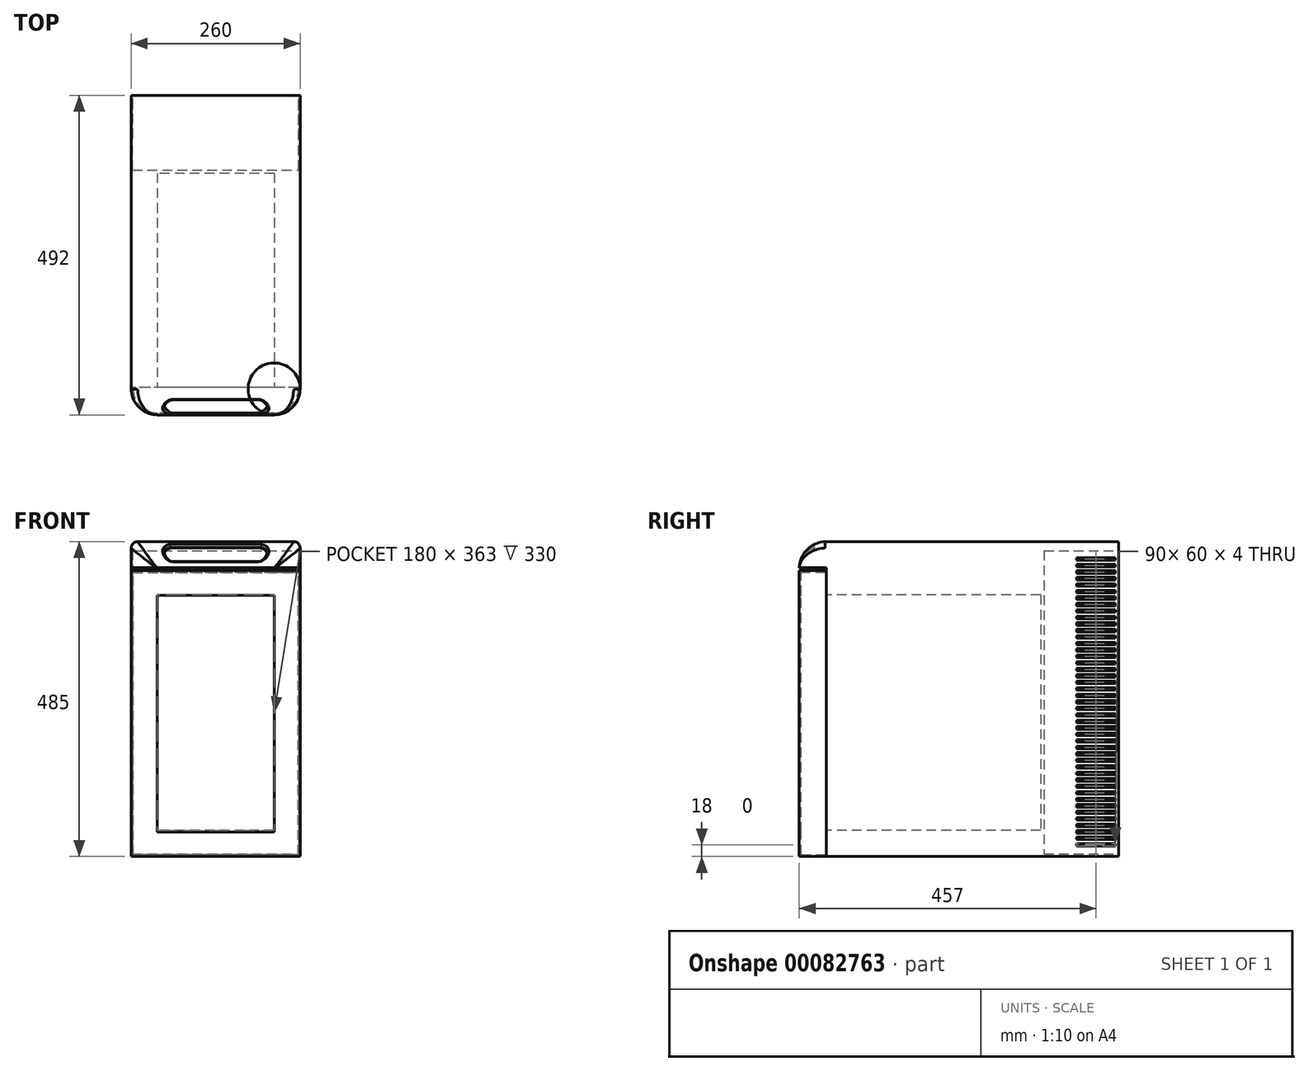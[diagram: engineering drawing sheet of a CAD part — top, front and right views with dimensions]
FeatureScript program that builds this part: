
annotation { "Feature Type Name" : "Feature", "Feature Type Description" : "" }
export const myFeature = defineFeature(function(context is Context, id is Id, definition is map)
    precondition{}
    {
        {
            var Q0;
            Q0=qCreatedBy(makeId("Top.planeOp"),FACE);
            var sketch = newSketch(context, id + "F0", { "sketchPlane" : qUnion([Q0])});
            skLineSegment(sketch, "E0.bottom", {"start": v(130, 225) * mm, "end": v(-130, 225) * mm});
            skLineSegment(sketch, "E0.top", {"start": v(130, -225) * mm, "end": v(-130, -225) * mm});
            skLineSegment(sketch, "E0.left", {"start": v(130, 225) * mm, "end": v(130, -225) * mm});
            skLineSegment(sketch, "E0.right", {"start": v(-130, 225) * mm, "end": v(-130, -225) * mm});
            skPoint(sketch, "E0.middle", {"position": v(0, 0) * mm});
            skSolve(sketch);
        }
        {
            var Q0;
            Q0 = qSketchRegion(id + "F0", true);
            extrude(context, id + "F1", {"entities" : qUnion([Q0]), "depth" : 485 * mm});
        }
        {
            var Q0;
            Q0=makeQuery(id+"F1.opExtrude","SWEPT_FACE",FACE,{"disambiguationData":[OSD([sQuery(id+"F0.wireOp",EDGE,"E0.right")])]});
            var sketch = newSketch(context, id + "F2", { "sketchPlane" : qUnion([Q0])});
            skLineSegment(sketch, "E1", {"start": v(225, 445) * mm, "end": v(267, 445) * mm});
            skLineSegment(sketch, "E2", {"start": v(225, 445) * mm, "end": v(225, 485) * mm});
            skLineSegment(sketch, "E3", {"start": v(225, 485) * mm, "end": v(-225, 485) * mm, "construction": true});
            skArc(sketch, "E4", {"start": v(225, 485) * mm, "mid": v(254, 473.4) * mm, "end": v(267, 445) * mm});
            skSolve(sketch);
        }
        {
            var Q0;
            Q0 = qSketchRegion(id + "F2", true);
            var Q1;
            Q1=makeQuery(id+"F1.opExtrude","SWEPT_FACE",FACE,{"disambiguationData":[OSD([sQuery(id+"F0.wireOp",EDGE,"E0.left")])]});
            extrude(context, id + "F3", {"entities" : qUnion([Q0]), "operationType" : NewBodyOperationType.ADD, "endBound" : BoundingType.UP_TO_SURFACE, "oppositeDirection" : true, "endBoundEntityFace" : qUnion([Q1]), "depth" : 25 * mm});
        }
        {
            var Q0;
            Q0=makeQuery(id+"F3.opExtrude","SWEPT_FACE",FACE,{"disambiguationData":[OSD([sQuery(id+"F2.wireOp",EDGE,"E1")])]});
            var sketch = newSketch(context, id + "F4", { "sketchPlane" : qUnion([Q0])});
            skLineSegment(sketch, "E5", {"start": v(0, 225) * mm, "end": v(0, 267) * mm, "construction": true});
            skArc(sketch, "E6", {"start": v(-130, 227) * mm, "mid": v(-118.28, 255.28) * mm, "end": v(-90, 267) * mm});
            skLineSegment(sketch, "E7", {"start": v(-130, 227) * mm, "end": v(-130, 267) * mm});
            skLineSegment(sketch, "E8", {"start": v(-130, 267) * mm, "end": v(-90, 267) * mm});
            skArc(sketch, "E9.MirrorCS", {"start": v(130, 227) * mm, "mid": v(118.28, 255.28) * mm, "end": v(90, 267) * mm});
            skLineSegment(sketch, "E10.MirrorCS", {"start": v(130, 227) * mm, "end": v(130, 267) * mm});
            skLineSegment(sketch, "E11.MirrorCS", {"start": v(130, 267) * mm, "end": v(90, 267) * mm});
            skSolve(sketch);
        }
        {
            var Q0;
            Q0 = qSketchRegion(id + "F4", true);
            extrude(context, id + "F5", {"entities" : qUnion([Q0]), "operationType" : NewBodyOperationType.REMOVE, "endBound" : BoundingType.THROUGH_ALL, "oppositeDirection" : true, "depth" : 25 * mm});
        }
        {
            var Q0;
            Q0=makeQuery(id+"F3.opExtrude","CAP_EDGE",EDGE,{"disambiguationData":[OSD([sQuery(id+"F2.wireOp",EDGE,"E4")])],"isStart":true});
            var Q1;
            Q1=makeQuery(id+"F5.boolean.opBoolean","INTERSECT",EDGE,{"derivedFrom":[makeQuery(id+"F3.opExtrude","SWEPT_FACE",FACE,{"disambiguationData":[OSD([sQuery(id+"F2.wireOp",EDGE,"E4")])]}),makeQuery(id+"F5.opExtrude","SWEPT_FACE",FACE,{"disambiguationData":[OSD([sQuery(id+"F4.wireOp",EDGE,"E6")])]})]});
            var Q2;
            Q2=makeQuery(id+"F3.opExtrude","CAP_EDGE",EDGE,{"disambiguationData":[OSD([sQuery(id+"F2.wireOp",EDGE,"E4")])],"isStart":false});
            var Q3;
            Q3=makeQuery(id+"F5.boolean.opBoolean","INTERSECT",EDGE,{"derivedFrom":[makeQuery(id+"F3.opExtrude","SWEPT_FACE",FACE,{"disambiguationData":[OSD([sQuery(id+"F2.wireOp",EDGE,"E4")])]}),makeQuery(id+"F5.opExtrude","SWEPT_FACE",FACE,{"disambiguationData":[OSD([sQuery(id+"F4.wireOp",EDGE,"E9.MirrorCS")])]})]});
            var Q4;
            Q4=makeQuery(id+"F1.opExtrude","CAP_EDGE",EDGE,{"disambiguationData":[OSD([sQuery(id+"F0.wireOp",EDGE,"E0.right")])],"isStart":false});
            var Q5;
            Q5=makeQuery(id+"F1.opExtrude","CAP_EDGE",EDGE,{"disambiguationData":[OSD([sQuery(id+"F0.wireOp",EDGE,"E0.left")])],"isStart":false});
            fillet(context, id + "F6", {"entities" : qUnion([Q0, Q1, Q2, Q3, Q4, Q5]), "radius" : 10 * mm, "allowEdgeOverflow" : false});
        }
        {
            var Q0;
            Q0=makeQuery(id+"F3.opExtrude","SWEPT_FACE",FACE,{"disambiguationData":[OSD([sQuery(id+"F2.wireOp",EDGE,"E1")])]});
            cPlane(context, id + "F7", {"entities" : qUnion([Q0]), "cplaneType" : CPlaneType.OFFSET, "offset" : 5 * mm, "width" : 150 * mm, "height" : 150 * mm});
        }
        {
            var Q0;
            Q0=qCreatedBy(id+"F7.planeOp",FACE);
            var sketch = newSketch(context, id + "F8", { "sketchPlane" : qUnion([Q0])});
            skLineSegment(sketch, "E12.0", {"start": v(90, 267) * mm, "end": v(-90, 267) * mm});
            skArc(sketch, "E12.1", {"start": v(130, 227) * mm, "mid": v(118.74, 254.82) * mm, "end": v(91.3, 266.98) * mm});
            skArc(sketch, "E12.2", {"start": v(91.3, 266.98) * mm, "mid": v(90.65, 267) * mm, "end": v(90, 267) * mm});
            skArc(sketch, "E12.3", {"start": v(-130, 227) * mm, "mid": v(-118.74, 254.82) * mm, "end": v(-91.3, 266.98) * mm});
            skArc(sketch, "E12.4", {"start": v(-91.3, 266.98) * mm, "mid": v(-90.65, 267) * mm, "end": v(-90, 267) * mm});
            skLineSegment(sketch, "E12.5", {"start": v(-130, 225) * mm, "end": v(-130, 227) * mm});
            skLineSegment(sketch, "E12.6", {"start": v(130, 225) * mm, "end": v(130, 227) * mm});
            skLineSegment(sketch, "E13", {"start": v(-130, 225) * mm, "end": v(130, 225) * mm});
            skSolve(sketch);
        }
        {
            var Q0;
            Q0 = qSketchRegion(id + "F8", true);
            var Q1;
            Q1=makeQuery(id+"F1.opExtrude","CAP_FACE",FACE,{"disambiguationData":[OSD([sQuery(id+"F0.wireOp",EDGE,"E0.bottom"),sQuery(id+"F0.wireOp",EDGE,"E0.top"),sQuery(id+"F0.wireOp",EDGE,"E0.left"),sQuery(id+"F0.wireOp",EDGE,"E0.right")])],"isStart":true});
            extrude(context, id + "F9", {"entities" : qUnion([Q0]), "endBound" : BoundingType.UP_TO_SURFACE, "endBoundEntityFace" : qUnion([Q1]), "depth" : 25 * mm});
        }
        {
            var Q0;
            Q0=makeQuery(id+"F9.opExtrude","SWEPT_FACE",FACE,{"disambiguationData":[OSD([sQuery(id+"F8.wireOp",EDGE,"E12.0")])]});
            var sketch = newSketch(context, id + "F10", { "sketchPlane" : qUnion([Q0])});
            skLineSegment(sketch, "E14.bottom", {"start": v(90, 402.22) * mm, "end": v(-90, 402.22) * mm});
            skLineSegment(sketch, "E14.top", {"start": v(90, 37.78) * mm, "end": v(-90, 37.78) * mm});
            skLineSegment(sketch, "E14.left", {"start": v(90, 402.22) * mm, "end": v(90, 37.78) * mm});
            skLineSegment(sketch, "E14.right", {"start": v(-90, 402.22) * mm, "end": v(-90, 37.78) * mm});
            skPoint(sketch, "E14.middle", {"position": v(0, 220) * mm});
            skPoint(sketch, "E14.middle.positionSnap0", {"position": v(-90, 220) * mm});
            skPoint(sketch, "E14.centerSnap0", {"position": v(-90, 220) * mm});
            skSolve(sketch);
        }
        {
            var Q0;
            Q0=makeQuery(id+"F9.opExtrude","SWEPT_FACE",FACE,{"disambiguationData":[OSD([sQuery(id+"F8.wireOp",EDGE,"E13")])]});
            shell(context, id + "F11", {"entities" : qUnion([Q0]), "thickness" : 3 * mm});
        }
        {
            var Q0;
            Q0 = qSketchRegion(id + "F10", true);
            extrude(context, id + "F12", {"entities" : qUnion([Q0]), "operationType" : NewBodyOperationType.REMOVE, "oppositeDirection" : true, "depth" : 3 * mm});
        }
        {
            var Q0;
            Q0=makeQuery(id+"F1.opExtrude","SWEPT_FACE",FACE,{"disambiguationData":[OSD([sQuery(id+"F0.wireOp",EDGE,"E0.top")])]});
            var sketch = newSketch(context, id + "F13", { "sketchPlane" : qUnion([Q0])});
            skLineSegment(sketch, "E15.bottom", {"start": v(90, 403) * mm, "end": v(-90, 403) * mm});
            skLineSegment(sketch, "E15.top", {"start": v(90, 40) * mm, "end": v(-90, 40) * mm});
            skLineSegment(sketch, "E15.left", {"start": v(90, 403) * mm, "end": v(90, 40) * mm});
            skLineSegment(sketch, "E15.right", {"start": v(-90, 403) * mm, "end": v(-90, 40) * mm});
            skPoint(sketch, "E15.middle", {"position": v(0, 221.5) * mm});
            skSolve(sketch);
        }
        {
            var Q0;
            Q0 = qSketchRegion(id + "F13", true);
            extrude(context, id + "F14", {"entities" : qUnion([Q0]), "operationType" : NewBodyOperationType.REMOVE, "oppositeDirection" : true, "depth" : 330 * mm});
        }
        {
            var Q0;
            {var subQ7=sQuery(id+"F8.wireOp",EDGE,"E12.0");Q0=makeQuery(id+"F12.boolean.opBoolean","SPLIT",FACE,{"disambiguationData":[TD([makeQuery(id+"F12.opExtrude","SWEPT_FACE",FACE,{"disambiguationData":[OSD([sQuery(id+"F10.wireOp",EDGE,"E14.top")])]})])],"derivedFrom":makeQuery(id+"F11.opShell","OFFSET_FACE",FACE,{"disambiguationData":[OSD([subQ7])]})});}
            var sketch = newSketch(context, id + "F15", { "sketchPlane" : qUnion([Q0])});
            skLineSegment(sketch, "E16.bottom", {"start": v(-90, 37.78) * mm, "end": v(90, 37.78) * mm});
            skLineSegment(sketch, "E16.top", {"start": v(-90, 402.22) * mm, "end": v(90, 402.22) * mm});
            skLineSegment(sketch, "E16.left", {"start": v(-90, 37.78) * mm, "end": v(-90, 402.22) * mm});
            skLineSegment(sketch, "E16.right", {"start": v(90, 37.78) * mm, "end": v(90, 402.22) * mm});
            skSolve(sketch);
        }
        {
            var Q0;
            Q0 = qSketchRegion(id + "F15", true);
            extrude(context, id + "F16", {"entities" : qUnion([Q0]), "oppositeDirection" : true, "depth" : 2 * mm});
        }
        {
            var Q0;
            Q0=makeQuery(id+"F3.boolean.opBoolean","MERGE",EDGE,{"derivedFrom":[makeQuery(id+"F1.opExtrude","CAP_EDGE",EDGE,{"disambiguationData":[OSD([sQuery(id+"F0.wireOp",EDGE,"E0.top")])],"isStart":false}),makeQuery(id+"F3.opExtrude","SWEPT_EDGE",EDGE,{"disambiguationData":[OSD([sQuery(id+"F0.wireOp",EDGE,"E0.right"),sQuery(id+"F2.wireOp",EDGE,"E2"),sQuery(id+"F2.wireOp",EDGE,"E4")])]})]});
            cPlane(context, id + "F17", {"entities" : qUnion([Q0]), "cplaneType" : CPlaneType.LINE_ANGLE, "offset" : 150 * mm, "angle" : 45 * degree, "width" : 150 * mm, "height" : 150 * mm});
        }
        {
            var Q0;
            Q0=qCreatedBy(id+"F17.planeOp",FACE);
            cPlane(context, id + "F18", {"entities" : qUnion([Q0]), "cplaneType" : CPlaneType.OFFSET, "offset" : 10 * mm, "width" : 150 * mm, "height" : 150 * mm});
        }
        {
            var Q0;
            Q0=qCreatedBy(id+"F18.planeOp",FACE);
            var sketch = newSketch(context, id + "F19", { "sketchPlane" : qUnion([Q0])});
            skLineSegment(sketch, "E17.bottom", {"start": v(-65.56, 164.16) * mm, "end": v(65.56, 164.16) * mm});
            skLineSegment(sketch, "E17.top", {"start": v(-65.56, 137.57) * mm, "end": v(65.56, 137.57) * mm});
            skPoint(sketch, "E17.middle", {"position": v(0, 150.87) * mm});
            skArc(sketch, "E18", {"start": v(-65.56, 137.57) * mm, "mid": v(-78.85, 150.87) * mm, "end": v(-65.56, 164.16) * mm});
            skArc(sketch, "E19", {"start": v(65.56, 137.57) * mm, "mid": v(78.85, 150.87) * mm, "end": v(65.56, 164.16) * mm});
            skSolve(sketch);
        }
        {
            var Q0;
            Q0 = qSketchRegion(id + "F19", true);
            extrude(context, id + "F20", {"entities" : qUnion([Q0]), "operationType" : NewBodyOperationType.REMOVE, "endBound" : BoundingType.SYMMETRIC, "depth" : 8 * mm});
        }
        {
            var Q0;
            Q0=makeQuery(id+"F20.boolean.opBoolean","INTERSECT",EDGE,{"derivedFrom":[makeQuery(id+"F3.opExtrude","SWEPT_FACE",FACE,{"disambiguationData":[OSD([sQuery(id+"F2.wireOp",EDGE,"E4")])]}),makeQuery(id+"F20.opExtrude","SWEPT_FACE",FACE,{"disambiguationData":[OSD([sQuery(id+"F19.wireOp",EDGE,"E18")])]})]});
            var Q1;
            Q1=makeQuery(id+"F20.boolean.opBoolean","INTERSECT",EDGE,{"derivedFrom":[makeQuery(id+"F3.opExtrude","SWEPT_FACE",FACE,{"disambiguationData":[OSD([sQuery(id+"F2.wireOp",EDGE,"E4")])]}),makeQuery(id+"F20.opExtrude","SWEPT_FACE",FACE,{"disambiguationData":[OSD([sQuery(id+"F19.wireOp",EDGE,"E19")])]})]});
            var Q2;
            Q2=makeQuery(id+"F20.boolean.opBoolean","INTERSECT",EDGE,{"derivedFrom":[makeQuery(id+"F3.opExtrude","SWEPT_FACE",FACE,{"disambiguationData":[OSD([sQuery(id+"F2.wireOp",EDGE,"E4")])]}),makeQuery(id+"F20.opExtrude","SWEPT_FACE",FACE,{"disambiguationData":[OSD([sQuery(id+"F19.wireOp",EDGE,"E17.bottom")])]})]});
            var Q3;
            Q3=makeQuery(id+"F20.boolean.opBoolean","INTERSECT",EDGE,{"derivedFrom":[makeQuery(id+"F3.opExtrude","SWEPT_FACE",FACE,{"disambiguationData":[OSD([sQuery(id+"F2.wireOp",EDGE,"E4")])]}),makeQuery(id+"F20.opExtrude","SWEPT_FACE",FACE,{"disambiguationData":[OSD([sQuery(id+"F19.wireOp",EDGE,"E17.top")])]})]});
            chamfer(context, id + "F21", {"entities" : qUnion([Q0, Q1, Q2, Q3]), "width" : 3 * mm, "tangentPropagation" : true});
        }
        {
            var Q0;
            Q0=makeQuery(id+"F1.opExtrude","SWEPT_FACE",FACE,{"disambiguationData":[OSD([sQuery(id+"F0.wireOp",EDGE,"E0.bottom")])]});
            var sketch = newSketch(context, id + "F22", { "sketchPlane" : qUnion([Q0])});
            skLineSegment(sketch, "E20.bottom", {"start": v(128, 471) * mm, "end": v(-128, 471) * mm});
            skLineSegment(sketch, "E20.top", {"start": v(128, 4) * mm, "end": v(-128, 4) * mm});
            skLineSegment(sketch, "E20.left", {"start": v(128, 471) * mm, "end": v(128, 4) * mm});
            skLineSegment(sketch, "E20.right", {"start": v(-128, 471) * mm, "end": v(-128, 4) * mm});
            skPoint(sketch, "E20.middle", {"position": v(0, 237.5) * mm});
            skPoint(sketch, "E20.middle.positionSnap0", {"position": v(-130, 237.5) * mm});
            skPoint(sketch, "E20.centerSnap0", {"position": v(-130, 237.5) * mm});
            skSolve(sketch);
        }
        {
            var Q0;
            Q0 = qSketchRegion(id + "F22", true);
            extrude(context, id + "F23", {"entities" : qUnion([Q0]), "operationType" : NewBodyOperationType.REMOVE, "oppositeDirection" : true, "depth" : (485 - 330 - 40) * mm});
        }
        {
            var Q0;
            Q0=makeQuery(id+"F3.boolean.opBoolean","MERGE",FACE,{"derivedFrom":[makeQuery(id+"F1.opExtrude","SWEPT_FACE",FACE,{"disambiguationData":[OSD([sQuery(id+"F0.wireOp",EDGE,"E0.left")])]}),makeQuery(id+"F3.opExtrude","CAP_FACE",FACE,{"disambiguationData":[OSD([sQuery(id+"F2.wireOp",EDGE,"E1"),sQuery(id+"F2.wireOp",EDGE,"E2"),sQuery(id+"F2.wireOp",EDGE,"E4")])],"isStart":false})]});
            var sketch = newSketch(context, id + "F24", { "sketchPlane" : qUnion([Q0])});
            skLineSegment(sketch, "E21.bottom", {"start": v(220, 460) * mm, "end": v(160, 460) * mm});
            skLineSegment(sketch, "E21.top", {"start": v(220, 456) * mm, "end": v(160, 456) * mm});
            skLineSegment(sketch, "E21.left", {"start": v(220, 460) * mm, "end": v(220, 456) * mm});
            skLineSegment(sketch, "E21.right", {"start": v(160, 460) * mm, "end": v(160, 456) * mm});
            skPoint(sketch, "E21.middle", {"position": v(190, 458) * mm});
            skPoint(sketch, "E22.0.1.0", {"position": v(190, 448) * mm});
            skLineSegment(sketch, "E22.0.1.1", {"start": v(220, 450) * mm, "end": v(160, 450) * mm});
            skLineSegment(sketch, "E22.0.1.2", {"start": v(220, 446) * mm, "end": v(160, 446) * mm});
            skLineSegment(sketch, "E22.0.1.3", {"start": v(220, 450) * mm, "end": v(220, 446) * mm});
            skLineSegment(sketch, "E22.0.1.4", {"start": v(160, 450) * mm, "end": v(160, 446) * mm});
            skPoint(sketch, "E22.0.2.0", {"position": v(190, 438) * mm});
            skLineSegment(sketch, "E22.0.2.1", {"start": v(220, 440) * mm, "end": v(160, 440) * mm});
            skLineSegment(sketch, "E22.0.2.2", {"start": v(220, 436) * mm, "end": v(160, 436) * mm});
            skLineSegment(sketch, "E22.0.2.3", {"start": v(220, 440) * mm, "end": v(220, 436) * mm});
            skLineSegment(sketch, "E22.0.2.4", {"start": v(160, 440) * mm, "end": v(160, 436) * mm});
            skPoint(sketch, "E22.0.3.0", {"position": v(190, 428) * mm});
            skLineSegment(sketch, "E22.0.3.1", {"start": v(220, 430) * mm, "end": v(160, 430) * mm});
            skLineSegment(sketch, "E22.0.3.2", {"start": v(220, 426) * mm, "end": v(160, 426) * mm});
            skLineSegment(sketch, "E22.0.3.3", {"start": v(220, 430) * mm, "end": v(220, 426) * mm});
            skLineSegment(sketch, "E22.0.3.4", {"start": v(160, 430) * mm, "end": v(160, 426) * mm});
            skPoint(sketch, "E22.0.4.0", {"position": v(190, 418) * mm});
            skLineSegment(sketch, "E22.0.4.1", {"start": v(220, 420) * mm, "end": v(160, 420) * mm});
            skLineSegment(sketch, "E22.0.4.2", {"start": v(220, 416) * mm, "end": v(160, 416) * mm});
            skLineSegment(sketch, "E22.0.4.3", {"start": v(220, 420) * mm, "end": v(220, 416) * mm});
            skLineSegment(sketch, "E22.0.4.4", {"start": v(160, 420) * mm, "end": v(160, 416) * mm});
            skPoint(sketch, "E22.0.5.0", {"position": v(190, 408) * mm});
            skLineSegment(sketch, "E22.0.5.1", {"start": v(220, 410) * mm, "end": v(160, 410) * mm});
            skLineSegment(sketch, "E22.0.5.2", {"start": v(220, 406) * mm, "end": v(160, 406) * mm});
            skLineSegment(sketch, "E22.0.5.3", {"start": v(220, 410) * mm, "end": v(220, 406) * mm});
            skLineSegment(sketch, "E22.0.5.4", {"start": v(160, 410) * mm, "end": v(160, 406) * mm});
            skPoint(sketch, "E22.0.6.0", {"position": v(190, 398) * mm});
            skLineSegment(sketch, "E22.0.6.1", {"start": v(220, 400) * mm, "end": v(160, 400) * mm});
            skLineSegment(sketch, "E22.0.6.2", {"start": v(220, 396) * mm, "end": v(160, 396) * mm});
            skLineSegment(sketch, "E22.0.6.3", {"start": v(220, 400) * mm, "end": v(220, 396) * mm});
            skLineSegment(sketch, "E22.0.6.4", {"start": v(160, 400) * mm, "end": v(160, 396) * mm});
            skPoint(sketch, "E22.0.7.0", {"position": v(190, 388) * mm});
            skLineSegment(sketch, "E22.0.7.1", {"start": v(220, 390) * mm, "end": v(160, 390) * mm});
            skLineSegment(sketch, "E22.0.7.2", {"start": v(220, 386) * mm, "end": v(160, 386) * mm});
            skLineSegment(sketch, "E22.0.7.3", {"start": v(220, 390) * mm, "end": v(220, 386) * mm});
            skLineSegment(sketch, "E22.0.7.4", {"start": v(160, 390) * mm, "end": v(160, 386) * mm});
            skPoint(sketch, "E22.0.8.0", {"position": v(190, 378) * mm});
            skLineSegment(sketch, "E22.0.8.1", {"start": v(220, 380) * mm, "end": v(160, 380) * mm});
            skLineSegment(sketch, "E22.0.8.2", {"start": v(220, 376) * mm, "end": v(160, 376) * mm});
            skLineSegment(sketch, "E22.0.8.3", {"start": v(220, 380) * mm, "end": v(220, 376) * mm});
            skLineSegment(sketch, "E22.0.8.4", {"start": v(160, 380) * mm, "end": v(160, 376) * mm});
            skPoint(sketch, "E22.0.9.0", {"position": v(190, 368) * mm});
            skLineSegment(sketch, "E22.0.9.1", {"start": v(220, 370) * mm, "end": v(160, 370) * mm});
            skLineSegment(sketch, "E22.0.9.2", {"start": v(220, 366) * mm, "end": v(160, 366) * mm});
            skLineSegment(sketch, "E22.0.9.3", {"start": v(220, 370) * mm, "end": v(220, 366) * mm});
            skLineSegment(sketch, "E22.0.9.4", {"start": v(160, 370) * mm, "end": v(160, 366) * mm});
            skPoint(sketch, "E22.0.10.0", {"position": v(190, 358) * mm});
            skLineSegment(sketch, "E22.0.10.1", {"start": v(220, 360) * mm, "end": v(160, 360) * mm});
            skLineSegment(sketch, "E22.0.10.2", {"start": v(220, 356) * mm, "end": v(160, 356) * mm});
            skLineSegment(sketch, "E22.0.10.3", {"start": v(220, 360) * mm, "end": v(220, 356) * mm});
            skLineSegment(sketch, "E22.0.10.4", {"start": v(160, 360) * mm, "end": v(160, 356) * mm});
            skPoint(sketch, "E22.0.11.0", {"position": v(190, 348) * mm});
            skLineSegment(sketch, "E22.0.11.1", {"start": v(220, 350) * mm, "end": v(160, 350) * mm});
            skLineSegment(sketch, "E22.0.11.2", {"start": v(220, 346) * mm, "end": v(160, 346) * mm});
            skLineSegment(sketch, "E22.0.11.3", {"start": v(220, 350) * mm, "end": v(220, 346) * mm});
            skLineSegment(sketch, "E22.0.11.4", {"start": v(160, 350) * mm, "end": v(160, 346) * mm});
            skPoint(sketch, "E22.0.12.0", {"position": v(190, 338) * mm});
            skLineSegment(sketch, "E22.0.12.1", {"start": v(220, 340) * mm, "end": v(160, 340) * mm});
            skLineSegment(sketch, "E22.0.12.2", {"start": v(220, 336) * mm, "end": v(160, 336) * mm});
            skLineSegment(sketch, "E22.0.12.3", {"start": v(220, 340) * mm, "end": v(220, 336) * mm});
            skLineSegment(sketch, "E22.0.12.4", {"start": v(160, 340) * mm, "end": v(160, 336) * mm});
            skPoint(sketch, "E22.0.13.0", {"position": v(190, 328) * mm});
            skLineSegment(sketch, "E22.0.13.1", {"start": v(220, 330) * mm, "end": v(160, 330) * mm});
            skLineSegment(sketch, "E22.0.13.2", {"start": v(220, 326) * mm, "end": v(160, 326) * mm});
            skLineSegment(sketch, "E22.0.13.3", {"start": v(220, 330) * mm, "end": v(220, 326) * mm});
            skLineSegment(sketch, "E22.0.13.4", {"start": v(160, 330) * mm, "end": v(160, 326) * mm});
            skPoint(sketch, "E22.0.14.0", {"position": v(190, 318) * mm});
            skLineSegment(sketch, "E22.0.14.1", {"start": v(220, 320) * mm, "end": v(160, 320) * mm});
            skLineSegment(sketch, "E22.0.14.2", {"start": v(220, 316) * mm, "end": v(160, 316) * mm});
            skLineSegment(sketch, "E22.0.14.3", {"start": v(220, 320) * mm, "end": v(220, 316) * mm});
            skLineSegment(sketch, "E22.0.14.4", {"start": v(160, 320) * mm, "end": v(160, 316) * mm});
            skPoint(sketch, "E22.0.15.0", {"position": v(190, 308) * mm});
            skLineSegment(sketch, "E22.0.15.1", {"start": v(220, 310) * mm, "end": v(160, 310) * mm});
            skLineSegment(sketch, "E22.0.15.2", {"start": v(220, 306) * mm, "end": v(160, 306) * mm});
            skLineSegment(sketch, "E22.0.15.3", {"start": v(220, 310) * mm, "end": v(220, 306) * mm});
            skLineSegment(sketch, "E22.0.15.4", {"start": v(160, 310) * mm, "end": v(160, 306) * mm});
            skPoint(sketch, "E22.0.16.0", {"position": v(190, 298) * mm});
            skLineSegment(sketch, "E22.0.16.1", {"start": v(220, 300) * mm, "end": v(160, 300) * mm});
            skLineSegment(sketch, "E22.0.16.2", {"start": v(220, 296) * mm, "end": v(160, 296) * mm});
            skLineSegment(sketch, "E22.0.16.3", {"start": v(220, 300) * mm, "end": v(220, 296) * mm});
            skLineSegment(sketch, "E22.0.16.4", {"start": v(160, 300) * mm, "end": v(160, 296) * mm});
            skPoint(sketch, "E22.0.17.0", {"position": v(190, 288) * mm});
            skLineSegment(sketch, "E22.0.17.1", {"start": v(220, 290) * mm, "end": v(160, 290) * mm});
            skLineSegment(sketch, "E22.0.17.2", {"start": v(220, 286) * mm, "end": v(160, 286) * mm});
            skLineSegment(sketch, "E22.0.17.3", {"start": v(220, 290) * mm, "end": v(220, 286) * mm});
            skLineSegment(sketch, "E22.0.17.4", {"start": v(160, 290) * mm, "end": v(160, 286) * mm});
            skPoint(sketch, "E22.0.18.0", {"position": v(190, 278) * mm});
            skLineSegment(sketch, "E22.0.18.1", {"start": v(220, 280) * mm, "end": v(160, 280) * mm});
            skLineSegment(sketch, "E22.0.18.2", {"start": v(220, 276) * mm, "end": v(160, 276) * mm});
            skLineSegment(sketch, "E22.0.18.3", {"start": v(220, 280) * mm, "end": v(220, 276) * mm});
            skLineSegment(sketch, "E22.0.18.4", {"start": v(160, 280) * mm, "end": v(160, 276) * mm});
            skPoint(sketch, "E22.0.19.0", {"position": v(190, 268) * mm});
            skLineSegment(sketch, "E22.0.19.1", {"start": v(220, 270) * mm, "end": v(160, 270) * mm});
            skLineSegment(sketch, "E22.0.19.2", {"start": v(220, 266) * mm, "end": v(160, 266) * mm});
            skLineSegment(sketch, "E22.0.19.3", {"start": v(220, 270) * mm, "end": v(220, 266) * mm});
            skLineSegment(sketch, "E22.0.19.4", {"start": v(160, 270) * mm, "end": v(160, 266) * mm});
            skPoint(sketch, "E22.0.20.0", {"position": v(190, 258) * mm});
            skLineSegment(sketch, "E22.0.20.1", {"start": v(220, 260) * mm, "end": v(160, 260) * mm});
            skLineSegment(sketch, "E22.0.20.2", {"start": v(220, 256) * mm, "end": v(160, 256) * mm});
            skLineSegment(sketch, "E22.0.20.3", {"start": v(220, 260) * mm, "end": v(220, 256) * mm});
            skLineSegment(sketch, "E22.0.20.4", {"start": v(160, 260) * mm, "end": v(160, 256) * mm});
            skPoint(sketch, "E22.0.21.0", {"position": v(190, 248) * mm});
            skLineSegment(sketch, "E22.0.21.1", {"start": v(220, 250) * mm, "end": v(160, 250) * mm});
            skLineSegment(sketch, "E22.0.21.2", {"start": v(220, 246) * mm, "end": v(160, 246) * mm});
            skLineSegment(sketch, "E22.0.21.3", {"start": v(220, 250) * mm, "end": v(220, 246) * mm});
            skLineSegment(sketch, "E22.0.21.4", {"start": v(160, 250) * mm, "end": v(160, 246) * mm});
            skPoint(sketch, "E22.0.22.0", {"position": v(190, 238) * mm});
            skLineSegment(sketch, "E22.0.22.1", {"start": v(220, 240) * mm, "end": v(160, 240) * mm});
            skLineSegment(sketch, "E22.0.22.2", {"start": v(220, 236) * mm, "end": v(160, 236) * mm});
            skLineSegment(sketch, "E22.0.22.3", {"start": v(220, 240) * mm, "end": v(220, 236) * mm});
            skLineSegment(sketch, "E22.0.22.4", {"start": v(160, 240) * mm, "end": v(160, 236) * mm});
            skPoint(sketch, "E22.0.23.0", {"position": v(190, 228) * mm});
            skLineSegment(sketch, "E22.0.23.1", {"start": v(220, 230) * mm, "end": v(160, 230) * mm});
            skLineSegment(sketch, "E22.0.23.2", {"start": v(220, 226) * mm, "end": v(160, 226) * mm});
            skLineSegment(sketch, "E22.0.23.3", {"start": v(220, 230) * mm, "end": v(220, 226) * mm});
            skLineSegment(sketch, "E22.0.23.4", {"start": v(160, 230) * mm, "end": v(160, 226) * mm});
            skPoint(sketch, "E22.0.24.0", {"position": v(190, 218) * mm});
            skLineSegment(sketch, "E22.0.24.1", {"start": v(220, 220) * mm, "end": v(160, 220) * mm});
            skLineSegment(sketch, "E22.0.24.2", {"start": v(220, 216) * mm, "end": v(160, 216) * mm});
            skLineSegment(sketch, "E22.0.24.3", {"start": v(220, 220) * mm, "end": v(220, 216) * mm});
            skLineSegment(sketch, "E22.0.24.4", {"start": v(160, 220) * mm, "end": v(160, 216) * mm});
            skPoint(sketch, "E22.0.25.0", {"position": v(190, 208) * mm});
            skLineSegment(sketch, "E22.0.25.1", {"start": v(220, 210) * mm, "end": v(160, 210) * mm});
            skLineSegment(sketch, "E22.0.25.2", {"start": v(220, 206) * mm, "end": v(160, 206) * mm});
            skLineSegment(sketch, "E22.0.25.3", {"start": v(220, 210) * mm, "end": v(220, 206) * mm});
            skLineSegment(sketch, "E22.0.25.4", {"start": v(160, 210) * mm, "end": v(160, 206) * mm});
            skPoint(sketch, "E22.0.26.0", {"position": v(190, 198) * mm});
            skLineSegment(sketch, "E22.0.26.1", {"start": v(220, 200) * mm, "end": v(160, 200) * mm});
            skLineSegment(sketch, "E22.0.26.2", {"start": v(220, 196) * mm, "end": v(160, 196) * mm});
            skLineSegment(sketch, "E22.0.26.3", {"start": v(220, 200) * mm, "end": v(220, 196) * mm});
            skLineSegment(sketch, "E22.0.26.4", {"start": v(160, 200) * mm, "end": v(160, 196) * mm});
            skPoint(sketch, "E22.0.27.0", {"position": v(190, 188) * mm});
            skLineSegment(sketch, "E22.0.27.1", {"start": v(220, 190) * mm, "end": v(160, 190) * mm});
            skLineSegment(sketch, "E22.0.27.2", {"start": v(220, 186) * mm, "end": v(160, 186) * mm});
            skLineSegment(sketch, "E22.0.27.3", {"start": v(220, 190) * mm, "end": v(220, 186) * mm});
            skLineSegment(sketch, "E22.0.27.4", {"start": v(160, 190) * mm, "end": v(160, 186) * mm});
            skPoint(sketch, "E22.0.28.0", {"position": v(190, 178) * mm});
            skLineSegment(sketch, "E22.0.28.1", {"start": v(220, 180) * mm, "end": v(160, 180) * mm});
            skLineSegment(sketch, "E22.0.28.2", {"start": v(220, 176) * mm, "end": v(160, 176) * mm});
            skLineSegment(sketch, "E22.0.28.3", {"start": v(220, 180) * mm, "end": v(220, 176) * mm});
            skLineSegment(sketch, "E22.0.28.4", {"start": v(160, 180) * mm, "end": v(160, 176) * mm});
            skPoint(sketch, "E22.0.29.0", {"position": v(190, 168) * mm});
            skLineSegment(sketch, "E22.0.29.1", {"start": v(220, 170) * mm, "end": v(160, 170) * mm});
            skLineSegment(sketch, "E22.0.29.2", {"start": v(220, 166) * mm, "end": v(160, 166) * mm});
            skLineSegment(sketch, "E22.0.29.3", {"start": v(220, 170) * mm, "end": v(220, 166) * mm});
            skLineSegment(sketch, "E22.0.29.4", {"start": v(160, 170) * mm, "end": v(160, 166) * mm});
            skPoint(sketch, "E22.0.30.0", {"position": v(190, 158) * mm});
            skLineSegment(sketch, "E22.0.30.1", {"start": v(220, 160) * mm, "end": v(160, 160) * mm});
            skLineSegment(sketch, "E22.0.30.2", {"start": v(220, 156) * mm, "end": v(160, 156) * mm});
            skLineSegment(sketch, "E22.0.30.3", {"start": v(220, 160) * mm, "end": v(220, 156) * mm});
            skLineSegment(sketch, "E22.0.30.4", {"start": v(160, 160) * mm, "end": v(160, 156) * mm});
            skPoint(sketch, "E22.0.31.0", {"position": v(190, 148) * mm});
            skLineSegment(sketch, "E22.0.31.1", {"start": v(220, 150) * mm, "end": v(160, 150) * mm});
            skLineSegment(sketch, "E22.0.31.2", {"start": v(220, 146) * mm, "end": v(160, 146) * mm});
            skLineSegment(sketch, "E22.0.31.3", {"start": v(220, 150) * mm, "end": v(220, 146) * mm});
            skLineSegment(sketch, "E22.0.31.4", {"start": v(160, 150) * mm, "end": v(160, 146) * mm});
            skPoint(sketch, "E22.0.32.0", {"position": v(190, 138) * mm});
            skLineSegment(sketch, "E22.0.32.1", {"start": v(220, 140) * mm, "end": v(160, 140) * mm});
            skLineSegment(sketch, "E22.0.32.2", {"start": v(220, 136) * mm, "end": v(160, 136) * mm});
            skLineSegment(sketch, "E22.0.32.3", {"start": v(220, 140) * mm, "end": v(220, 136) * mm});
            skLineSegment(sketch, "E22.0.32.4", {"start": v(160, 140) * mm, "end": v(160, 136) * mm});
            skPoint(sketch, "E22.0.33.0", {"position": v(190, 128) * mm});
            skLineSegment(sketch, "E22.0.33.1", {"start": v(220, 130) * mm, "end": v(160, 130) * mm});
            skLineSegment(sketch, "E22.0.33.2", {"start": v(220, 126) * mm, "end": v(160, 126) * mm});
            skLineSegment(sketch, "E22.0.33.3", {"start": v(220, 130) * mm, "end": v(220, 126) * mm});
            skLineSegment(sketch, "E22.0.33.4", {"start": v(160, 130) * mm, "end": v(160, 126) * mm});
            skPoint(sketch, "E22.0.34.0", {"position": v(190, 118) * mm});
            skLineSegment(sketch, "E22.0.34.1", {"start": v(220, 120) * mm, "end": v(160, 120) * mm});
            skLineSegment(sketch, "E22.0.34.2", {"start": v(220, 116) * mm, "end": v(160, 116) * mm});
            skLineSegment(sketch, "E22.0.34.3", {"start": v(220, 120) * mm, "end": v(220, 116) * mm});
            skLineSegment(sketch, "E22.0.34.4", {"start": v(160, 120) * mm, "end": v(160, 116) * mm});
            skPoint(sketch, "E22.0.35.0", {"position": v(190, 108) * mm});
            skLineSegment(sketch, "E22.0.35.1", {"start": v(220, 110) * mm, "end": v(160, 110) * mm});
            skLineSegment(sketch, "E22.0.35.2", {"start": v(220, 106) * mm, "end": v(160, 106) * mm});
            skLineSegment(sketch, "E22.0.35.3", {"start": v(220, 110) * mm, "end": v(220, 106) * mm});
            skLineSegment(sketch, "E22.0.35.4", {"start": v(160, 110) * mm, "end": v(160, 106) * mm});
            skPoint(sketch, "E22.0.36.0", {"position": v(190, 98) * mm});
            skLineSegment(sketch, "E22.0.36.1", {"start": v(220, 100) * mm, "end": v(160, 100) * mm});
            skLineSegment(sketch, "E22.0.36.2", {"start": v(220, 96) * mm, "end": v(160, 96) * mm});
            skLineSegment(sketch, "E22.0.36.3", {"start": v(220, 100) * mm, "end": v(220, 96) * mm});
            skLineSegment(sketch, "E22.0.36.4", {"start": v(160, 100) * mm, "end": v(160, 96) * mm});
            skPoint(sketch, "E22.0.37.0", {"position": v(190, 88) * mm});
            skLineSegment(sketch, "E22.0.37.1", {"start": v(220, 90) * mm, "end": v(160, 90) * mm});
            skLineSegment(sketch, "E22.0.37.2", {"start": v(220, 86) * mm, "end": v(160, 86) * mm});
            skLineSegment(sketch, "E22.0.37.3", {"start": v(220, 90) * mm, "end": v(220, 86) * mm});
            skLineSegment(sketch, "E22.0.37.4", {"start": v(160, 90) * mm, "end": v(160, 86) * mm});
            skPoint(sketch, "E22.0.38.0", {"position": v(190, 78) * mm});
            skLineSegment(sketch, "E22.0.38.1", {"start": v(220, 80) * mm, "end": v(160, 80) * mm});
            skLineSegment(sketch, "E22.0.38.2", {"start": v(220, 76) * mm, "end": v(160, 76) * mm});
            skLineSegment(sketch, "E22.0.38.3", {"start": v(220, 80) * mm, "end": v(220, 76) * mm});
            skLineSegment(sketch, "E22.0.38.4", {"start": v(160, 80) * mm, "end": v(160, 76) * mm});
            skPoint(sketch, "E22.0.39.0", {"position": v(190, 68) * mm});
            skLineSegment(sketch, "E22.0.39.1", {"start": v(220, 70) * mm, "end": v(160, 70) * mm});
            skLineSegment(sketch, "E22.0.39.2", {"start": v(220, 66) * mm, "end": v(160, 66) * mm});
            skLineSegment(sketch, "E22.0.39.3", {"start": v(220, 70) * mm, "end": v(220, 66) * mm});
            skLineSegment(sketch, "E22.0.39.4", {"start": v(160, 70) * mm, "end": v(160, 66) * mm});
            skPoint(sketch, "E22.0.40.0", {"position": v(190, 58) * mm});
            skLineSegment(sketch, "E22.0.40.1", {"start": v(220, 60) * mm, "end": v(160, 60) * mm});
            skLineSegment(sketch, "E22.0.40.2", {"start": v(220, 56) * mm, "end": v(160, 56) * mm});
            skLineSegment(sketch, "E22.0.40.3", {"start": v(220, 60) * mm, "end": v(220, 56) * mm});
            skLineSegment(sketch, "E22.0.40.4", {"start": v(160, 60) * mm, "end": v(160, 56) * mm});
            skPoint(sketch, "E22.0.41.0", {"position": v(190, 48) * mm});
            skLineSegment(sketch, "E22.0.41.1", {"start": v(220, 50) * mm, "end": v(160, 50) * mm});
            skLineSegment(sketch, "E22.0.41.2", {"start": v(220, 46) * mm, "end": v(160, 46) * mm});
            skLineSegment(sketch, "E22.0.41.3", {"start": v(220, 50) * mm, "end": v(220, 46) * mm});
            skLineSegment(sketch, "E22.0.41.4", {"start": v(160, 50) * mm, "end": v(160, 46) * mm});
            skPoint(sketch, "E22.0.42.0", {"position": v(190, 38) * mm});
            skLineSegment(sketch, "E22.0.42.1", {"start": v(220, 40) * mm, "end": v(160, 40) * mm});
            skLineSegment(sketch, "E22.0.42.2", {"start": v(220, 36) * mm, "end": v(160, 36) * mm});
            skLineSegment(sketch, "E22.0.42.3", {"start": v(220, 40) * mm, "end": v(220, 36) * mm});
            skLineSegment(sketch, "E22.0.42.4", {"start": v(160, 40) * mm, "end": v(160, 36) * mm});
            skPoint(sketch, "E22.0.43.0", {"position": v(190, 28) * mm});
            skLineSegment(sketch, "E22.0.43.1", {"start": v(220, 30) * mm, "end": v(160, 30) * mm});
            skLineSegment(sketch, "E22.0.43.2", {"start": v(220, 26) * mm, "end": v(160, 26) * mm});
            skLineSegment(sketch, "E22.0.43.3", {"start": v(220, 30) * mm, "end": v(220, 26) * mm});
            skLineSegment(sketch, "E22.0.43.4", {"start": v(160, 30) * mm, "end": v(160, 26) * mm});
            skPoint(sketch, "E22.0.44.0", {"position": v(190, 18) * mm});
            skLineSegment(sketch, "E22.0.44.1", {"start": v(220, 20) * mm, "end": v(160, 20) * mm});
            skLineSegment(sketch, "E22.0.44.2", {"start": v(220, 16) * mm, "end": v(160, 16) * mm});
            skLineSegment(sketch, "E22.0.44.3", {"start": v(220, 20) * mm, "end": v(220, 16) * mm});
            skLineSegment(sketch, "E22.0.44.4", {"start": v(160, 20) * mm, "end": v(160, 16) * mm});
            skLineSegment(sketch, "E22.direction1", {"start": v(190, 458) * mm, "end": v(215, 458) * mm, "construction": true});
            skLineSegment(sketch, "E22.direction2", {"start": v(190, 458) * mm, "end": v(190, 448) * mm, "construction": true});
            skSolve(sketch);
        }
        {
            var Q0;
            Q0 = qSketchRegion(id + "F24", true);
            extrude(context, id + "F25", {"entities" : qUnion([Q0]), "operationType" : NewBodyOperationType.REMOVE, "endBound" : BoundingType.THROUGH_ALL, "oppositeDirection" : true, "depth" : 25 * mm});
        }
    });
